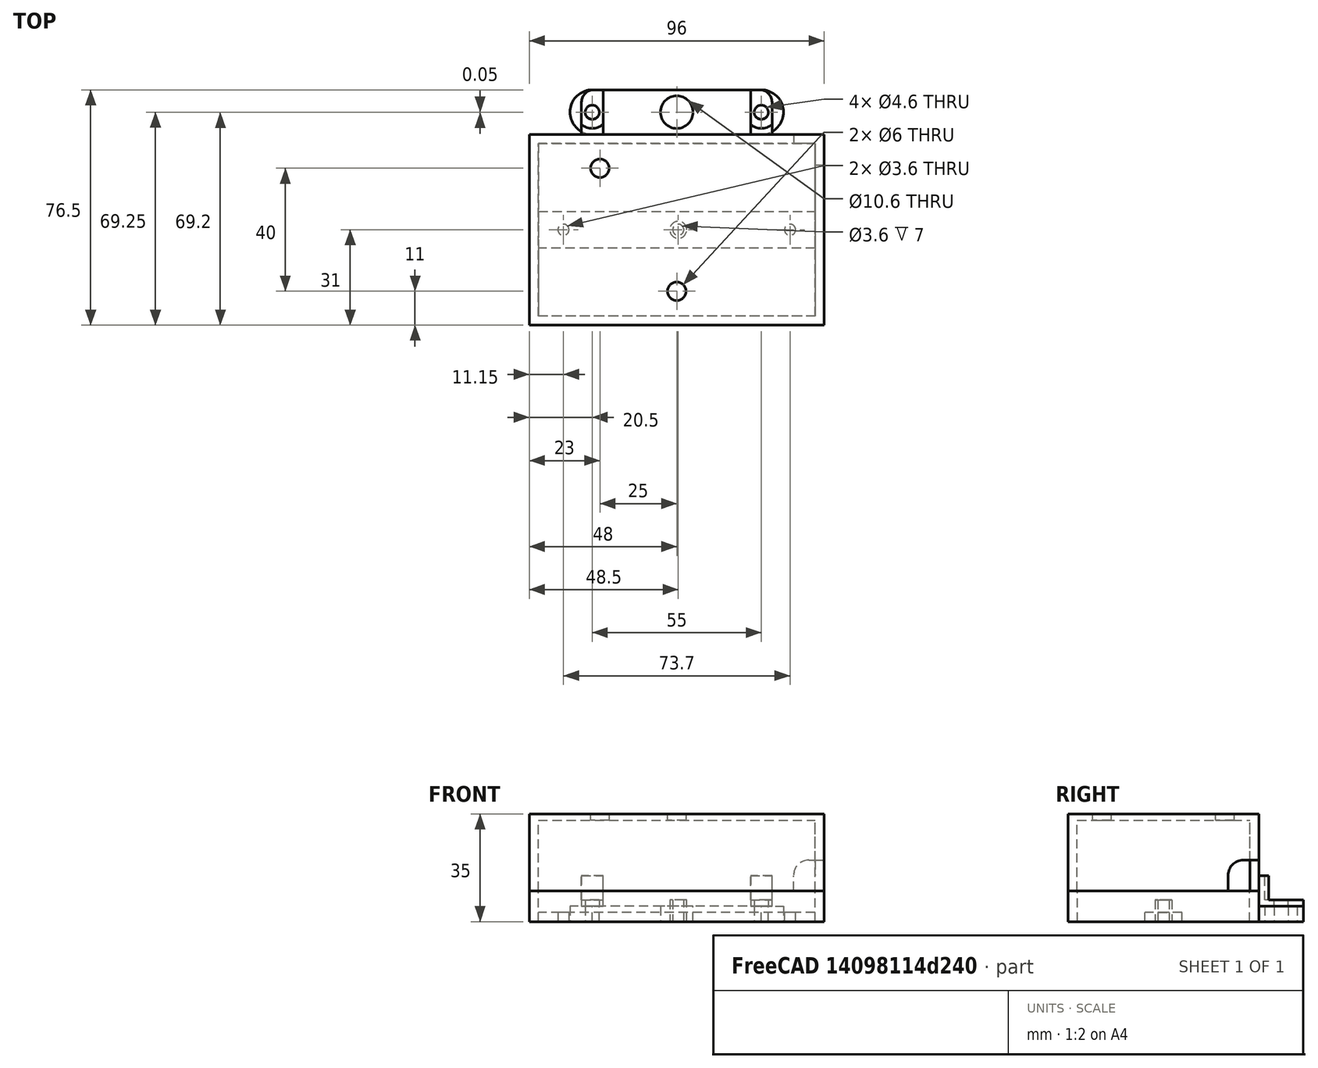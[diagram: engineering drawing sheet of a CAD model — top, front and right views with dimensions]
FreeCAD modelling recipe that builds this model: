
FCSTD DOCUMENT  (FreeCAD 1.1R44227 +568 (Git))
Label: circuit_housing
License: All rights reserved
LicenseURL: https://en.wikipedia.org/wiki/All_rights_reserved
objects: Sketcher::SketchObject×11, PartDesign::Pocket×7, PartDesign::Pad×4, App::Point×4, PartDesign::Body×3, Mesh::Feature×3, PartDesign::Fillet×2, App::Part×1
note: 64 computed .brp shape members not serialized (recipe doc carries the construction recipe); baked Part::Feature solids carry a one-line shape summary decoded from their .brp

FEATURE [Sketcher::SketchObject] Sketch
  ArcFitTolerance = 1e-06
  AttachmentSupport = -> [XY_Plane001]
  ExternalTypes = [0]
  FullyConstrained = true
  MakeInternals = false
  MapMode = 5
  _ExternalGeoVersion = 0
  sketch-geometry (23):
    g0: LineSegment StartX=-48 StartY=31 StartZ=0 EndX=-48 EndY=-31 EndZ=0
    g1: LineSegment StartX=-48 StartY=-31 StartZ=0 EndX=48 EndY=-31 EndZ=0
    g2: LineSegment StartX=48 StartY=-31 StartZ=0 EndX=48 EndY=31 EndZ=0
    g3: LineSegment [constr] StartX=48 StartY=31 StartZ=0 EndX=-48 EndY=31 EndZ=0
    g4: LineSegment StartX=-45 StartY=28 StartZ=0 EndX=-45 EndY=6 EndZ=0
    g5: LineSegment StartX=-45 StartY=6 StartZ=0 EndX=45 EndY=6 EndZ=0
    g6: LineSegment StartX=45 StartY=6 StartZ=0 EndX=45 EndY=28 EndZ=0
    g7: LineSegment StartX=45 StartY=28 StartZ=0 EndX=-45 EndY=28 EndZ=0
    g8: LineSegment StartX=-45 StartY=-6 StartZ=0 EndX=-45 EndY=-28 EndZ=0
    g9: LineSegment StartX=-45 StartY=-28 StartZ=0 EndX=45 EndY=-28 EndZ=0
    g10: LineSegment StartX=45 StartY=-28 StartZ=0 EndX=45 EndY=-6 EndZ=0
    g11: LineSegment StartX=45 StartY=-6 StartZ=0 EndX=-45 EndY=-6 EndZ=0
    g12: Circle CenterX=-36.85 CenterY=0 CenterZ=0 NormalX=0 NormalY=0 NormalZ=1 AngleXU=0 Radius=1.8
    g13: Circle CenterX=36.85 CenterY=0 CenterZ=0 NormalX=0 NormalY=0 NormalZ=1 AngleXU=0 Radius=1.8
    g14: ArcOfCircle CenterX=-27.5 CenterY=38.25 CenterZ=0 NormalX=0 NormalY=0 NormalZ=1 AngleXU=0 Radius=7.25 StartAngle=1.5708 EndAngle=4.71239
    g15: ArcOfCircle CenterX=27.5 CenterY=38.25 CenterZ=0 NormalX=0 NormalY=0 NormalZ=1 AngleXU=0 Radius=7.25 StartAngle=4.71239 EndAngle=7.85398
    g16: LineSegment StartX=-27.5 StartY=45.5 StartZ=0 EndX=27.5 EndY=45.5 EndZ=0
    g17: LineSegment [constr] StartX=-27.5 StartY=31 StartZ=0 EndX=27.5 EndY=31 EndZ=0
    g18: Circle CenterX=-27.5 CenterY=38.25 CenterZ=0 NormalX=0 NormalY=0 NormalZ=1 AngleXU=0 Radius=2.3
    g19: Circle CenterX=27.5 CenterY=38.25 CenterZ=0 NormalX=0 NormalY=0 NormalZ=1 AngleXU=0 Radius=2.3
    g20: Circle CenterX=0 CenterY=38.25 CenterZ=0 NormalX=0 NormalY=0 NormalZ=1 AngleXU=0 Radius=5.3
    g21: LineSegment StartX=-48 StartY=31 StartZ=0 EndX=-27.5 EndY=31 EndZ=0
    g22: LineSegment StartX=48 StartY=31 StartZ=0 EndX=27.5 EndY=31 EndZ=0
  constraints (58):
    c: Coincident(g0,g1)
    c: Coincident(g1,g2)
    c: Coincident(g2,g3)
    c: Coincident(g3,g0)
    c: Vertical(g0)
    c: Vertical(g2)
    c: Horizontal(g1)
    c: Horizontal(g3)
    c: Symmetric(g0,g1,g-1)
    c: DistanceX(g3,g3) = 96
    c: DistanceY(g2,g2) = 62
    c: Coincident(g4,g5)
    c: Coincident(g5,g6)
    c: Coincident(g6,g7)
    c: Coincident(g7,g4)
    c: Vertical(g4)
    c: Vertical(g6)
    c: Horizontal(g5)
    c: Horizontal(g7)
    c: Coincident(g8,g9)
    c: Coincident(g9,g10)
    c: Coincident(g10,g11)
    c: Coincident(g11,g8)
    c: Vertical(g8)
    c: Vertical(g10)
    c: Horizontal(g9)
    c: Horizontal(g11)
    c: Symmetric(g8,g4,g-1)
    c: Equal(g4,g8)
    c: Equal(g5,g11)
    c: DistanceX(g0,g4) = 3
    c: DistanceX(g6,g2) = 3
    c: DistanceY(g1,g9) = 3
    c: DistanceY(g10,g5) = 12
    c: PointOnObject(g12,g-1)
    c: Symmetric(g12,g13,g-2)
    c: Equal(g12,g13)
    c: DistanceX(g12,g13) = 73.7
    c: Diameter(g12) = 3.6
    c: Tangent(g14,g16) = 1.5708
    c: Tangent(g14,g17) = -1.5708
    c: Tangent(g15,g16) = 1.5708
    c: Tangent(g15,g17) = -1.5708
    c: Equal(g14,g15)
    c: Symmetric(g14,g15,g-2)
    c: Coincident(g18,g14)
    c: Coincident(g19,g15)
    c: PointOnObject(g20,g-2)
    c: Equal(g18,g19)
    c: Diameter(g20) = 10.6
    c: DistanceX(g16,g16) = 55
    c: DistanceY(g20,g15) = 0
    c: Diameter(g14) = 14.5
    c: Diameter(g18) = 4.6
    c: Coincident(g21,g0)
    c: Coincident(g21,g14)
    c: Coincident(g22,g2)
    c: Tangent(g22,g15) = 1.5708
FEATURE [PartDesign::Pad] Pad
  Direction = (0,0,1)
  Length = 10
  Length2 = 10
  Profile = -> Sketch
  ReferenceAxis = -> Sketch [N_Axis]
  Refine = true
  SideType = 0
  Suppressed = false
  Type = 0
  Type2 = 0
FEATURE [Sketcher::SketchObject] Sketch001
  ArcFitTolerance = 1e-06
  AttachmentSupport = -> [Pad]
  ExternalGeometry = -> [Pad]
  ExternalTypes = [0]
  FullyConstrained = true
  MakeInternals = false
  MapMode = 5
  Placement = pos=(0,0,10) rot=(0,0,1;0rad)
  _ExternalGeoVersion = 0
  sketch-geometry (4):
    g0: LineSegment StartX=-45 StartY=6 StartZ=0 EndX=-45 EndY=-6 EndZ=0
    g1: LineSegment StartX=-45 StartY=-6 StartZ=0 EndX=45 EndY=-6 EndZ=0
    g2: LineSegment StartX=45 StartY=-6 StartZ=0 EndX=45 EndY=6 EndZ=0
    g3: LineSegment StartX=45 StartY=6 StartZ=0 EndX=-45 EndY=6 EndZ=0
  constraints (10):
    c: Coincident(g0,g1)
    c: Coincident(g1,g2)
    c: Coincident(g2,g3)
    c: Coincident(g3,g0)
    c: Vertical(g0)
    c: Vertical(g2)
    c: Horizontal(g1)
    c: Horizontal(g3)
    c: Coincident(g1,g-4)
    c: Coincident(g0,g-3)
FEATURE [PartDesign::Pocket] Pocket
  BaseFeature = -> Pad
  Direction = (0,0,-1)
  Length = 7
  Length2 = 5
  Profile = -> Sketch001
  ReferenceAxis = -> Sketch001 [N_Axis]
  Refine = true
  SideType = 0
  Suppressed = false
  Type = 0
  Type2 = 0
FEATURE [Sketcher::SketchObject] Sketch002
  ArcFitTolerance = 1e-06
  AttachmentSupport = -> [Pocket]
  ExternalGeometry = -> [Pocket]
  ExternalTypes = [0]
  FullyConstrained = true
  MakeInternals = false
  MapMode = 5
  Placement = pos=(0,0,10) rot=(0,0,1;0rad)
  _ExternalGeoVersion = 0
  sketch-geometry (4):
    g0: LineSegment StartX=-35 StartY=45.5 StartZ=0 EndX=-35 EndY=31 EndZ=0
    g1: LineSegment StartX=-35 StartY=31 StartZ=0 EndX=35 EndY=31 EndZ=0
    g2: LineSegment StartX=35 StartY=31 StartZ=0 EndX=35 EndY=45.5 EndZ=0
    g3: LineSegment StartX=35 StartY=45.5 StartZ=0 EndX=-35 EndY=45.5 EndZ=0
  constraints (12):
    c: Coincident(g0,g1)
    c: Coincident(g1,g2)
    c: Coincident(g2,g3)
    c: Coincident(g3,g0)
    c: Vertical(g0)
    c: Vertical(g2)
    c: Horizontal(g1)
    c: Horizontal(g3)
    c: PointOnObject(g-4,g3)
    c: PointOnObject(g-3,g1)
    c: DistanceX(g0,g-1) = 35
    c: DistanceX(g-1,g2) = 35
FEATURE [PartDesign::Pocket] Pocket001
  BaseFeature = -> Pocket
  Direction = (0,0,-1)
  Length = 5
  Length2 = 5
  Profile = -> Sketch002
  ReferenceAxis = -> Sketch002 [N_Axis]
  Refine = true
  SideType = 0
  Suppressed = false
  Type = 0
  Type2 = 0
FEATURE [PartDesign::Body] Body  label="Body_circuit_housing"
  AllowCompound = false
  Group = -> [Sketch,Pad,Sketch001,Pocket,Sketch002,Pocket001]
  Origin = -> Origin001
  Tip = -> Pocket001
FEATURE [Mesh::Feature] Mesh  label="Body_circuit_housing (Meshed)"
FEATURE [Sketcher::SketchObject] Sketch003
  ArcFitTolerance = 1e-06
  AttachmentSupport = -> [XY_Plane002]
  ExternalTypes = [0]
  FullyConstrained = true
  MakeInternals = false
  MapMode = 5
  _ExternalGeoVersion = 0
  sketch-geometry (2):
    g0: Circle CenterX=0.5 CenterY=0 CenterZ=0 NormalX=0 NormalY=0 NormalZ=1 AngleXU=0 Radius=2.75
    g1: Circle CenterX=0.5 CenterY=0 CenterZ=0 NormalX=0 NormalY=0 NormalZ=1 AngleXU=0 Radius=1.8
  constraints (4):
    c: Symmetric(g-1,g-1,g0)
    c: Coincident(g1,g0)
    c: Diameter(g1) = 3.6
    c: Diameter(g0) = 5.5
FEATURE [PartDesign::Pad] Pad001
  Direction = (0,0,1)
  Length = 7
  Length2 = 10
  Profile = -> Sketch003
  ReferenceAxis = -> Sketch003 [N_Axis]
  Refine = true
  SideType = 0
  Suppressed = false
  Type = 0
  Type2 = 0
FEATURE [PartDesign::Body] Body001  label="Body_Elevateur"
  AllowCompound = false
  Group = -> [Sketch003,Pad001]
  Origin = -> Origin002
  Tip = -> Pad001
FEATURE [App::Part] Part
  Group = -> [Body,Body001]
  Origin = -> Origin
FEATURE [Mesh::Feature] Mesh001  label="Body_Elevateur (Meshed)"
FEATURE [App::Point] Origin003  label="Origin"
  Role = Origin
FEATURE [App::Point] Origin004  label="Origin"
  Role = Origin
FEATURE [App::Point] Origin005  label="Origin"
  Role = Origin
FEATURE [App::Point] Origin007
  Role = Origin
FEATURE [Sketcher::SketchObject] Sketch004
  ArcFitTolerance = 1e-06
  AttachmentSupport = -> [Origin006]
  ExternalTypes = [0]
  FullyConstrained = true
  MakeInternals = false
  MapMode = 5
  _ExternalGeoVersion = 1
  sketch-geometry (4):
    g0: LineSegment StartX=-48 StartY=31 StartZ=0 EndX=-48 EndY=-31 EndZ=0
    g1: LineSegment StartX=-48 StartY=-31 StartZ=0 EndX=48 EndY=-31 EndZ=0
    g2: LineSegment StartX=48 StartY=-31 StartZ=0 EndX=48 EndY=31 EndZ=0
    g3: LineSegment StartX=48 StartY=31 StartZ=0 EndX=-48 EndY=31 EndZ=0
  constraints (11):
    c: Coincident(g0,g1)
    c: Coincident(g1,g2)
    c: Coincident(g2,g3)
    c: Coincident(g3,g0)
    c: Vertical(g0)
    c: Vertical(g2)
    c: Horizontal(g1)
    c: Horizontal(g3)
    c: Symmetric(g0,g1,g-1)
    c: DistanceX(g3,g3) = 96
    c: DistanceY(g0,g0) = 62
FEATURE [PartDesign::Pad] Pad002
  Direction = (0,0,1)
  Length = 25
  Length2 = 10
  Profile = -> Sketch004
  ReferenceAxis = -> Sketch004 [N_Axis]
  Refine = true
  SideType = 0
  Suppressed = false
  Type = 0
  Type2 = 0
FEATURE [Sketcher::SketchObject] Sketch005
  ArcFitTolerance = 1e-06
  AttachmentSupport = -> [Pad002]
  ExternalTypes = [0]
  FullyConstrained = true
  MakeInternals = false
  MapMode = 5
  Placement = pos=(0,0,0) rot=(1,0,0;3.14159rad)
  _ExternalGeoVersion = 1
  sketch-geometry (4):
    g0: LineSegment StartX=-45.05 StartY=28.1 StartZ=0 EndX=-45.05 EndY=-28.1 EndZ=0
    g1: LineSegment StartX=-45.05 StartY=-28.1 StartZ=0 EndX=45.05 EndY=-28.1 EndZ=0
    g2: LineSegment StartX=45.05 StartY=-28.1 StartZ=0 EndX=45.05 EndY=28.1 EndZ=0
    g3: LineSegment StartX=45.05 StartY=28.1 StartZ=0 EndX=-45.05 EndY=28.1 EndZ=0
  constraints (11):
    c: Coincident(g0,g1)
    c: Coincident(g1,g2)
    c: Coincident(g2,g3)
    c: Coincident(g3,g0)
    c: Vertical(g0)
    c: Vertical(g2)
    c: Horizontal(g1)
    c: Horizontal(g3)
    c: Symmetric(g0,g1,g-1)
    c: DistanceX(g3,g3) = 90.1
    c: DistanceY(g0,g0) = 56.2
FEATURE [PartDesign::Pocket] Pocket002
  BaseFeature = -> Pad002
  Direction = (0,0,1)
  Length = 23
  Length2 = 5
  Profile = -> Sketch005
  ReferenceAxis = -> Sketch005 [N_Axis]
  Refine = true
  SideType = 0
  Suppressed = false
  Type = 0
  Type2 = 0
FEATURE [Sketcher::SketchObject] Sketch006
  ArcFitTolerance = 1e-06
  AttachmentSupport = -> [Pocket002]
  ExternalTypes = [0]
  FullyConstrained = true
  MakeInternals = false
  MapMode = 5
  Placement = pos=(0,31,0) rot=(0,0.707107,0.707107;3.14159rad)
  _ExternalGeoVersion = 1
  sketch-geometry (8):
    g0: LineSegment StartX=-31 StartY=-5 StartZ=0 EndX=-31 EndY=5 EndZ=0
    g1: LineSegment StartX=-31 StartY=5 StartZ=0 EndX=-24 EndY=5 EndZ=0
    g2: LineSegment StartX=-24 StartY=5 StartZ=0 EndX=-24 EndY=-5 EndZ=0
    g3: LineSegment StartX=-24 StartY=-5 StartZ=0 EndX=-31 EndY=-5 EndZ=0
    g4: LineSegment StartX=24 StartY=-5 StartZ=0 EndX=24 EndY=5 EndZ=0
    g5: LineSegment StartX=24 StartY=5 StartZ=0 EndX=31 EndY=5 EndZ=0
    g6: LineSegment StartX=31 StartY=5 StartZ=0 EndX=31 EndY=-5 EndZ=0
    g7: LineSegment StartX=31 StartY=-5 StartZ=0 EndX=24 EndY=-5 EndZ=0
  constraints (23):
    c: Coincident(g0,g1)
    c: Coincident(g1,g2)
    c: Coincident(g2,g3)
    c: Coincident(g3,g0)
    c: Vertical(g0)
    c: Vertical(g2)
    c: Horizontal(g1)
    c: Horizontal(g3)
    c: Coincident(g4,g5)
    c: Coincident(g5,g6)
    c: Coincident(g6,g7)
    c: Coincident(g7,g4)
    c: Vertical(g4)
    c: Vertical(g6)
    c: Horizontal(g5)
    c: Horizontal(g7)
    c: Symmetric(g2,g4,g-2)
    c: DistanceX(g1,g4) = 48
    c: DistanceX(g3,g3) = 7
    c: Equal(g7,g3)
    c: Equal(g0,g4)
    c: DistanceY(g0,g0) = 10
    c: DistanceY(g2,g-1) = 5
FEATURE [PartDesign::Pad] Pad003
  BaseFeature = -> Pocket002
  Direction = (0,1,-2e-16)
  Length = 14.5
  Length2 = 10
  Profile = -> Sketch006
  ReferenceAxis = -> Sketch006 [N_Axis]
  Refine = true
  SideType = 0
  Suppressed = false
  Type = 0
  Type2 = 0
FEATURE [Sketcher::SketchObject] Sketch007
  ArcFitTolerance = 1e-06
  AttachmentSupport = -> [Pad003]
  ExternalTypes = [0]
  FullyConstrained = true
  MakeInternals = false
  MapMode = 5
  Placement = pos=(0,-1.1e-15,-5) rot=(1,0,0;3.14159rad)
  _ExternalGeoVersion = 1
  sketch-geometry (2):
    g0: Circle CenterX=-27.5 CenterY=-38.2 CenterZ=0 NormalX=0 NormalY=0 NormalZ=1 AngleXU=0 Radius=2.3
    g1: Circle CenterX=27.5 CenterY=-38.2 CenterZ=0 NormalX=0 NormalY=0 NormalZ=1 AngleXU=0 Radius=2.3
  constraints (5):
    c: Symmetric(g1,g0,g-2)
    c: Equal(g0,g1)
    c: DistanceX(g1) = 27.5
    c: Diameter(g0) = 4.6
    c: DistanceY(g0,g-1) = 38.2
FEATURE [PartDesign::Pocket] Pocket003
  BaseFeature = -> Pad003
  Direction = (0,0,1)
  Length = 5
  Length2 = 5
  Profile = -> Sketch007
  ReferenceAxis = -> Sketch007 [N_Axis]
  Refine = true
  SideType = 2
  Suppressed = false
  Type = 1
  Type2 = 0
FEATURE [Sketcher::SketchObject] Sketch008
  ArcFitTolerance = 1e-06
  ExternalTypes = [0]
  FullyConstrained = true
  MakeInternals = false
  MapMode = 5
  Placement = pos=(0,31,0) rot=(0,0.707107,0.707107;3.14159rad)
  _ExternalGeoVersion = 1
  sketch-geometry (4):
    g0: LineSegment StartX=-48 StartY=10 StartZ=0 EndX=-48 EndY=0 EndZ=0
    g1: LineSegment StartX=-48 StartY=0 StartZ=0 EndX=-38 EndY=0 EndZ=0
    g2: LineSegment StartX=-38 StartY=0 StartZ=0 EndX=-38 EndY=10 EndZ=0
    g3: LineSegment StartX=-38 StartY=10 StartZ=0 EndX=-48 EndY=10 EndZ=0
  constraints (12):
    c: Coincident(g0,g1)
    c: Coincident(g1,g2)
    c: Coincident(g2,g3)
    c: Coincident(g3,g0)
    c: Vertical(g0)
    c: Vertical(g2)
    c: Horizontal(g1)
    c: Horizontal(g3)
    c: PointOnObject(g-3,g0)
    c: DistanceY(g0,g0) = 10
    c: PointOnObject(g0,g-1)
    c: DistanceX(g3,g3) = 10
FEATURE [PartDesign::Pocket] Pocket004
  BaseFeature = -> Pocket003
  Direction = (0,-1,2e-16)
  Length = 10
  Length2 = 5
  Profile = -> Sketch008
  ReferenceAxis = -> Sketch008 [N_Axis]
  Refine = true
  SideType = 0
  Suppressed = false
  Type = 0
  Type2 = 0
FEATURE [PartDesign::Fillet] Fillet001
  Base = -> Pocket004 [Edge53,Edge56]
  BaseFeature = -> Pocket004
  Radius = 5
  Refine = true
  SupportTransform = false
  Suppressed = false
  UseAllEdges = false
FEATURE [Sketcher::SketchObject] Sketch009
  ArcFitTolerance = 1e-06
  AttachmentSupport = -> [Pocket004]
  ExternalGeometry = -> [Pocket004]
  ExternalTypes = [0,0]
  FullyConstrained = true
  MakeInternals = false
  MapMode = 5
  Placement = pos=(0,1.1e-15,5) rot=(0,0,1;0rad)
  _ExternalGeoVersion = 1
  sketch-geometry (6):
    g0: ArcOfCircle CenterX=-27.5 CenterY=38.2 CenterZ=0 NormalX=0 NormalY=0 NormalZ=1 AngleXU=0 Radius=5.25 StartAngle=2.83175 EndAngle=6.59303
    g1: ArcOfCircle CenterX=27.5 CenterY=38.2 CenterZ=0 NormalX=0 NormalY=0 NormalZ=1 AngleXU=0 Radius=5.25 StartAngle=2.83175 EndAngle=6.59303
    g2: LineSegment StartX=-32.5 StartY=46.8008 StartZ=0 EndX=-32.5 EndY=39.8008 EndZ=0
    g3: LineSegment StartX=32.5 StartY=39.8008 StartZ=0 EndX=32.5 EndY=46.8008 EndZ=0
    g4: LineSegment StartX=32.5 StartY=46.8008 StartZ=0 EndX=-32.5 EndY=46.8008 EndZ=0
    g5: LineSegment StartX=-22.5 StartY=39.8008 StartZ=0 EndX=22.5 EndY=39.8008 EndZ=0
  constraints (18):
    c: Coincident(g1,g-4)
    c: Coincident(g-3,g0)
    c: Coincident(g3,g4)
    c: Coincident(g4,g2)
    c: Vertical(g2)
    c: Vertical(g3)
    c: Horizontal(g4)
    c: Horizontal(g5)
    c: DistanceX(g5,g5) = 45
    c: DistanceX(g4,g4) = 65
    c: DistanceY(g2,g2) = 7
    c: Equal(g2,g3)
    c: Diameter(g0) = 10.5
    c: Coincident(g2,g0)
    c: Coincident(g5,g0)
    c: Coincident(g3,g1)
    c: Coincident(g5,g1)
    c: Equal(g0,g1)
FEATURE [PartDesign::Pocket] Pocket005
  BaseFeature = -> Fillet001
  Direction = (0,0,-1)
  Length = 8
  Length2 = 5
  Profile = -> Sketch009
  ReferenceAxis = -> Sketch009 [N_Axis]
  Refine = true
  SideType = 0
  Suppressed = false
  Type = 0
  Type2 = 0
FEATURE [PartDesign::Fillet] Fillet
  Base = -> Pocket005 [Edge46,Edge52]
  BaseFeature = -> Pocket005
  Radius = 4
  Refine = true
  SupportTransform = false
  Suppressed = false
  UseAllEdges = false
FEATURE [Sketcher::SketchObject] Sketch010
  ArcFitTolerance = 1e-06
  AttachmentSupport = -> [Fillet]
  ExternalTypes = [0]
  FullyConstrained = true
  MakeInternals = false
  MapMode = 5
  Placement = pos=(0,0,25) rot=(0,0,1;0rad)
  _ExternalGeoVersion = 1
  sketch-geometry (2):
    g0: Circle CenterX=0 CenterY=-20 CenterZ=0 NormalX=0 NormalY=0 NormalZ=1 AngleXU=0 Radius=3
    g1: Circle CenterX=-25 CenterY=20 CenterZ=0 NormalX=0 NormalY=0 NormalZ=1 AngleXU=0 Radius=3
  constraints (6):
    c: PointOnObject(g0,g-2)
    c: Equal(g0,g1)
    c: DistanceY(g0,g-1) = 20
    c: Diameter(g0) = 6
    c: DistanceX(g1,g-1) = 25
    c: DistanceY(g-1,g1) = 20
FEATURE [PartDesign::Pocket] Pocket006
  BaseFeature = -> Fillet
  Direction = (0,0,-1)
  Length = 5
  Length2 = 5
  Profile = -> Sketch010
  ReferenceAxis = -> Sketch010 [N_Axis]
  Refine = true
  SideType = 0
  Suppressed = false
  Type = 0
  Type2 = 0
FEATURE [PartDesign::Body] Body002  label="Body_Circuit_Roof"
  AllowCompound = false
  Group = -> [Sketch004,Pad002,Sketch005,Pocket002,Sketch006,Pad003,Sketch007,Pocket003,Sketch008,Pocket004,Fillet001,Sketch009,Pocket005,Fillet,Sketch010,Pocket006]
  Origin = -> Origin006
  Placement = pos=(0,0,10) rot=(0,0,1;0rad)
  Tip = -> Pocket006
FEATURE [Mesh::Feature] Mesh002  label="Body_Circuit_Roof (Meshed)"
